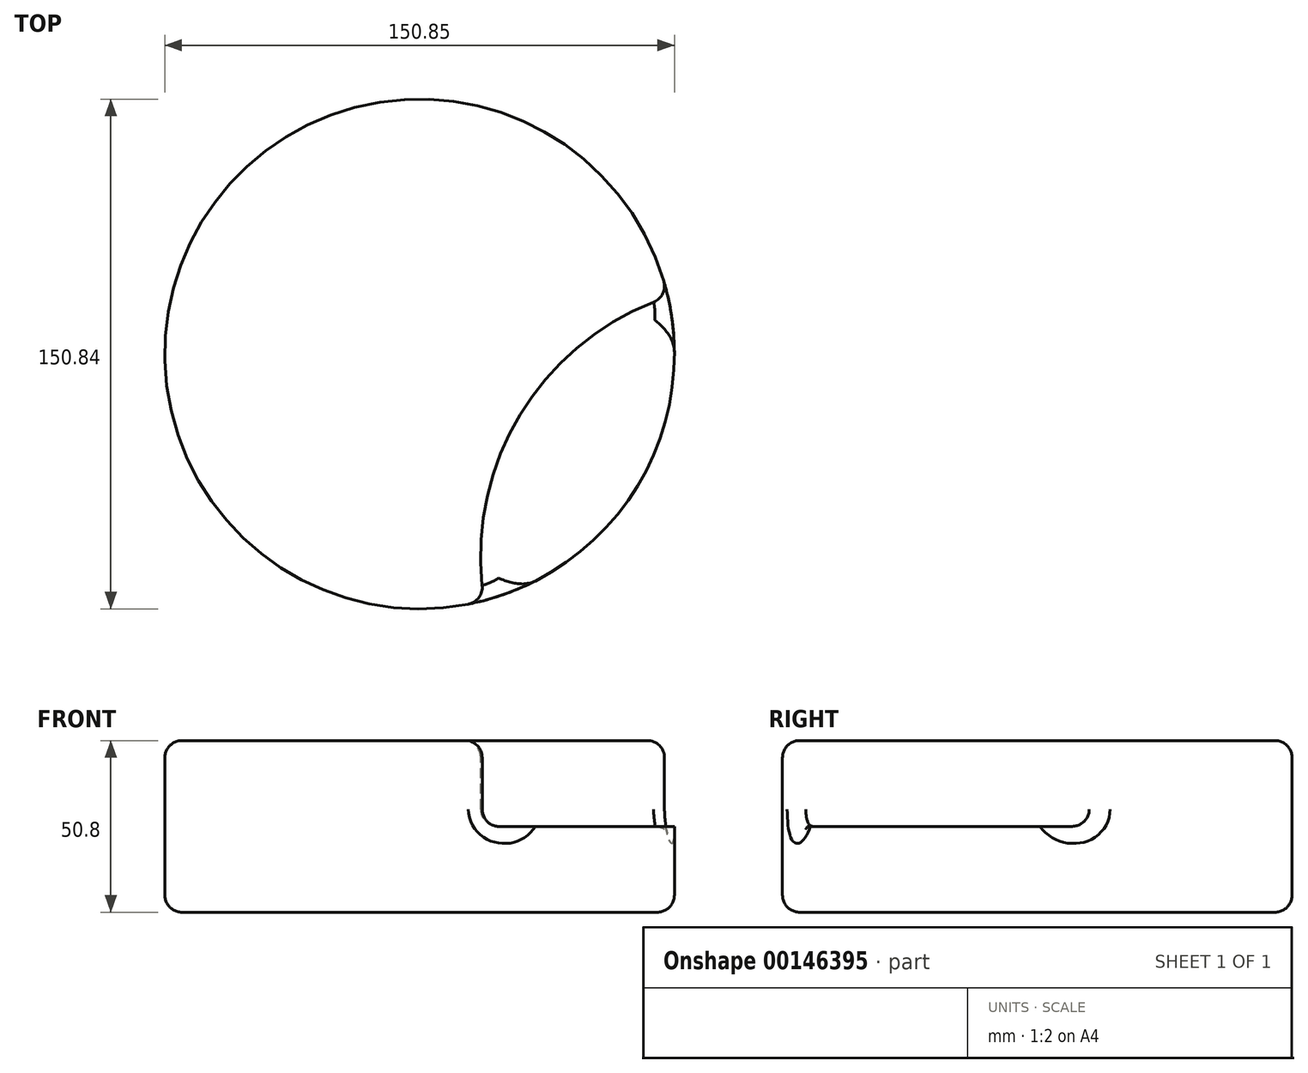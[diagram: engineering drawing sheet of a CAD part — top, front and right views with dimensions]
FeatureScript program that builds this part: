
annotation { "Feature Type Name" : "Feature", "Feature Type Description" : "" }
export const myFeature = defineFeature(function(context is Context, id is Id, definition is map)
    precondition{}
    {
        {
            var Q0;
            Q0=qCreatedBy(makeId("Top.planeOp"),FACE);
            var sketch = newSketch(context, id + "F0", { "sketchPlane" : qUnion([Q0])});
            skCircle(sketch, "E0", {"center": v(13.1, 0) * mm, "radius": 75.42 * mm});
            skSolve(sketch);
        }
        {
            var Q0;
            Q0 = qSketchRegion(id + "F0", true);
            extrude(context, id + "F2", {"entities" : qUnion([Q0]), "depth" : 50.8 * mm});
        }
        {
            var Q0;
            Q0=makeQuery(id+"F2.opExtrude","CAP_FACE",FACE,{"disambiguationData":[OSD([sQuery(id+"F0.wireOp",EDGE,"E0")])],"isStart":false});
            var sketch = newSketch(context, id + "F3", { "sketchPlane" : qUnion([Q0])});
            skCircle(sketch, "E1", {"center": v(112.06, -59.87) * mm, "radius": 80.9 * mm});
            skSolve(sketch);
        }
        {
            var Q0;
            Q0 = qSketchRegion(id + "F3", true);
            extrude(context, id + "F4", {"entities" : qUnion([Q0]), "operationType" : NewBodyOperationType.REMOVE, "oppositeDirection" : true, "depth" : 25.4 * mm});
        }
        {
            var Q0;
            Q0=makeQuery(id+"F2.opExtrude","CAP_FACE",FACE,{"disambiguationData":[OSD([sQuery(id+"F0.wireOp",EDGE,"E0")])],"isStart":false});
            var Q1;
            Q1=makeQuery(id+"F4.boolean.opBoolean","COPY",FACE,{"derivedFrom":makeQuery(id+"F4.opExtrude","SWEPT_FACE",FACE,{"disambiguationData":[OSD([sQuery(id+"F3.wireOp",EDGE,"E1")])]})});
            var Q2;
            Q2=makeQuery(id+"F2.opExtrude","CAP_FACE",FACE,{"disambiguationData":[OSD([sQuery(id+"F0.wireOp",EDGE,"E0")])],"isStart":true});
            fillet(context, id + "F1", {"entities" : qUnion([Q0, Q1, Q2]), "radius" : 5.08 * mm, "tangentPropagation" : true, "allowEdgeOverflow" : false});
        }
    });
